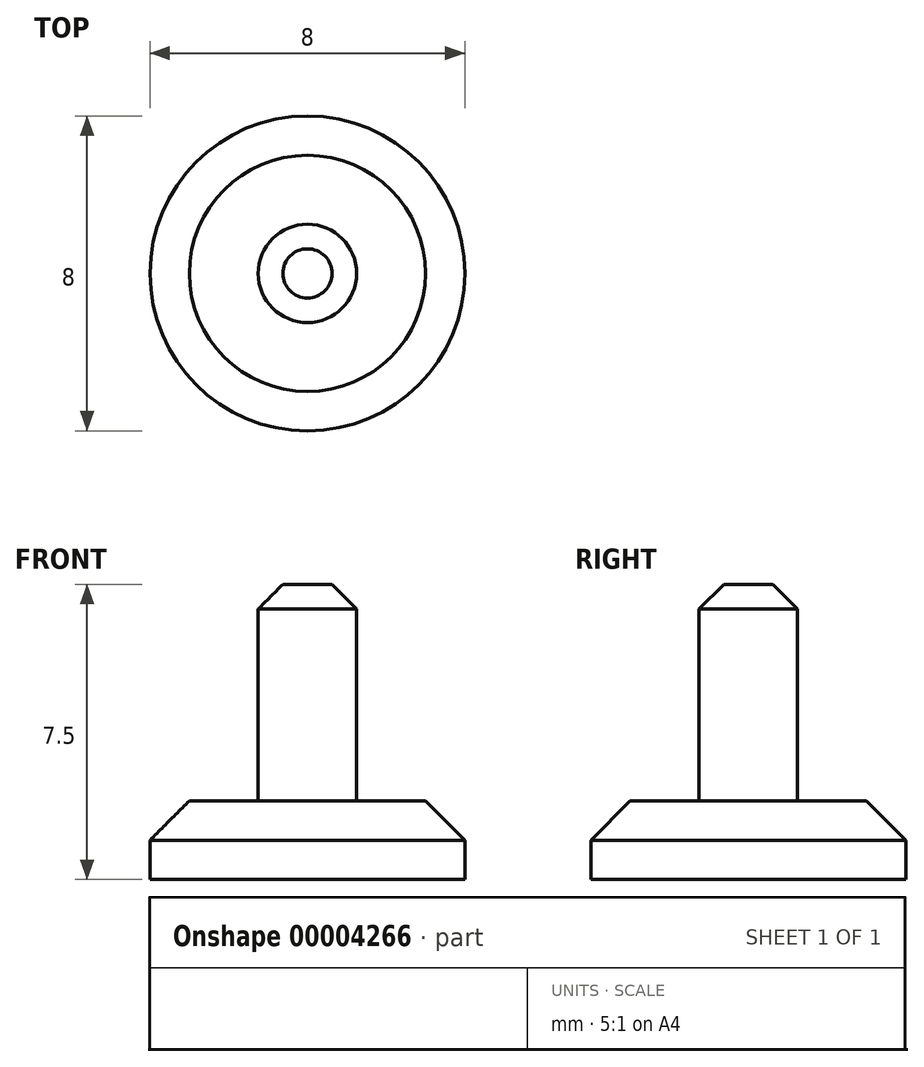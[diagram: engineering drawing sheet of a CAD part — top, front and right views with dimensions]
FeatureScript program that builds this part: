
annotation { "Feature Type Name" : "Feature", "Feature Type Description" : "" }
export const myFeature = defineFeature(function(context is Context, id is Id, definition is map)
    precondition{}
    {
        {
            var Q0;
            Q0=qCreatedBy(makeId("Front.planeOp"),FACE);
            var sketch = newSketch(context, id + "F0", { "sketchPlane" : qUnion([Q0])});
            skLineSegment(sketch, "E0", {"start": v(-9.53, 0) * mm, "end": v(0, 0) * mm, "construction": true});
            skLineSegment(sketch, "E1", {"start": v(0, 0) * mm, "end": v(0, 10.57) * mm, "construction": true});
            skLineSegment(sketch, "E2", {"start": v(0, 0) * mm, "end": v(0, 7.5) * mm});
            skLineSegment(sketch, "E3", {"start": v(0, 7.5) * mm, "end": v(-0.63, 7.5) * mm});
            skLineSegment(sketch, "E4", {"start": v(-1.25, 7.5) * mm, "end": v(-1.25, 6.88) * mm, "construction": true});
            skLineSegment(sketch, "E5", {"start": v(-4, 2) * mm, "end": v(-4, 1) * mm, "construction": true});
            skLineSegment(sketch, "E6", {"start": v(-4, 0) * mm, "end": v(0, 0) * mm});
            skLineSegment(sketch, "E7", {"start": v(0, 0) * mm, "end": v(9.53, 0) * mm, "construction": true});
            skLineSegment(sketch, "E8", {"start": v(-0.63, 7.5) * mm, "end": v(-1.25, 6.88) * mm});
            skLineSegment(sketch, "E9", {"start": v(-0.63, 7.5) * mm, "end": v(-1.25, 7.5) * mm, "construction": true});
            skLineSegment(sketch, "E10", {"start": v(-1.25, 6.88) * mm, "end": v(-1.25, 2) * mm});
            skLineSegment(sketch, "E11", {"start": v(-4, 1) * mm, "end": v(-3, 2) * mm});
            skLineSegment(sketch, "E12", {"start": v(-4, 1) * mm, "end": v(-4, 0) * mm});
            skLineSegment(sketch, "E13", {"start": v(-3, 2) * mm, "end": v(-1.25, 2) * mm});
            skLineSegment(sketch, "E14", {"start": v(-3, 2) * mm, "end": v(-4, 2) * mm, "construction": true});
            skSolve(sketch);
        }
        {
            var Q0;
            Q0=makeQuery(id+"F0.imprint","IMPRINT",FACE,{"disambiguationData":[TD([[makeQuery(id+"F0.imprint","IMPRINT",EDGE,{"derivedFrom":sQuery(id+"F0.wireOp",EDGE,"E2")}),1.0]])]});
            var Q1;
            Q1=sQuery(id+"F0.wireOp",EDGE,"E1");
            revolve(context, id + "F1", {"entities" : qUnion([Q0]), "axis" : qUnion([Q1]), "revolveType" : RevolveType.FULL});
        }
    });
